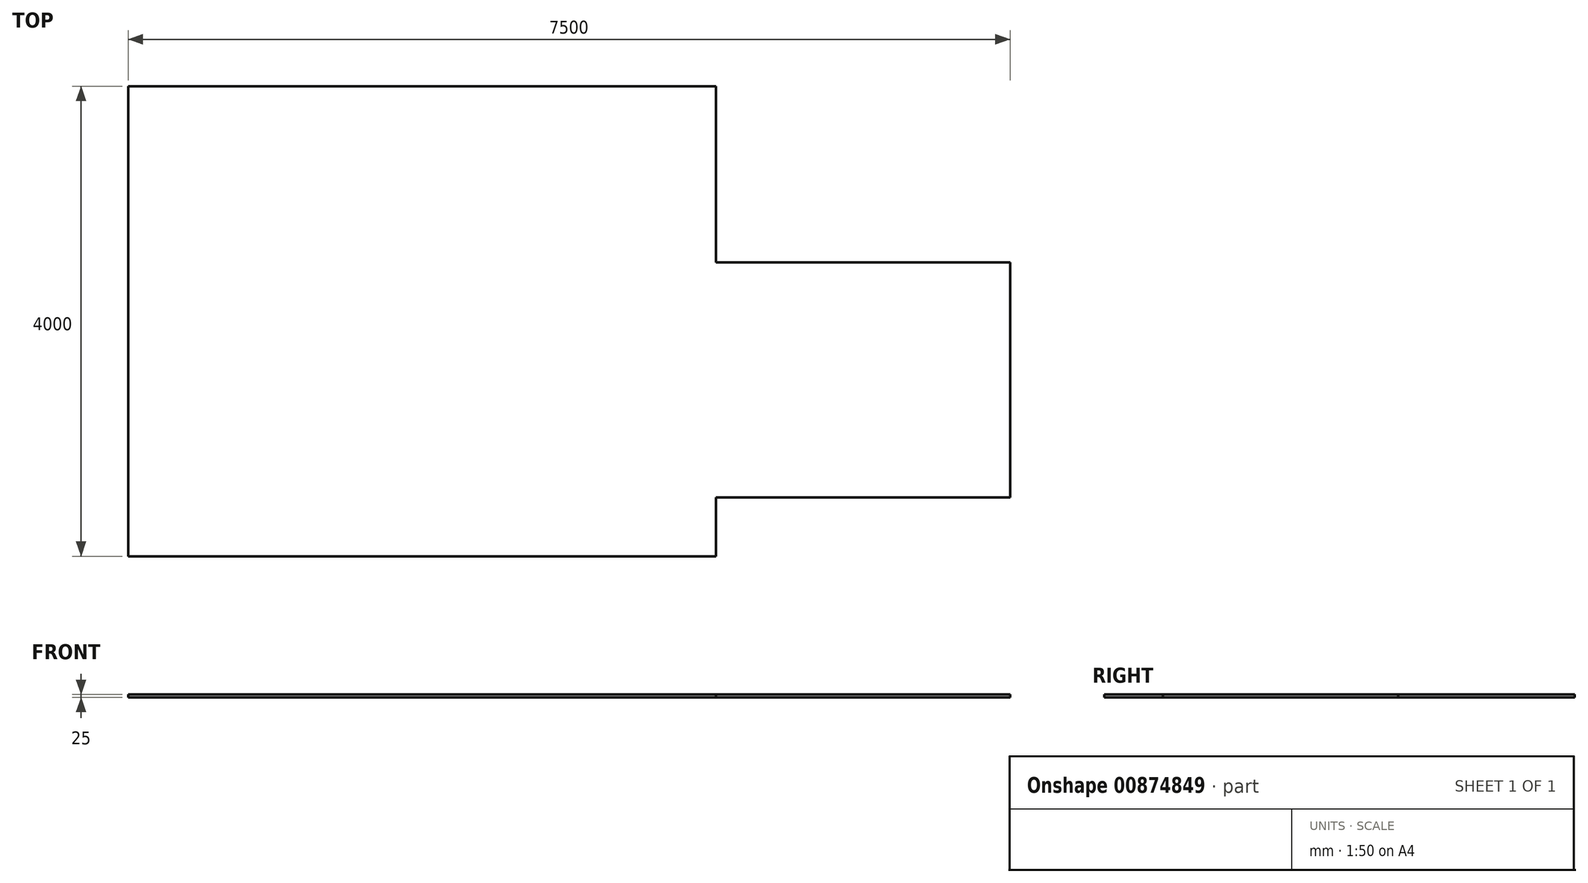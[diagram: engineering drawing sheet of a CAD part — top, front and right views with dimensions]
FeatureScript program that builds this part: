
annotation { "Feature Type Name" : "Feature", "Feature Type Description" : "" }
export const myFeature = defineFeature(function(context is Context, id is Id, definition is map)
    precondition{}
    {
        {
            var Q0;
            Q0=qCreatedBy(makeId("Top.planeOp"),FACE);
            var sketch = newSketch(context, id + "F0", { "sketchPlane" : qUnion([Q0])});
            skLineSegment(sketch, "E0.bottom", {"start": v(0, 0) * mm, "end": v(5000, 0) * mm});
            skLineSegment(sketch, "E0.top", {"start": v(0, 4000) * mm, "end": v(5000, 4000) * mm});
            skLineSegment(sketch, "E0.left", {"start": v(0, 0) * mm, "end": v(0, 4000) * mm});
            skLineSegment(sketch, "E0.right", {"start": v(5000, 0) * mm, "end": v(5000, 4000) * mm});
            skLineSegment(sketch, "E1.bottom", {"start": v(5000, 500) * mm, "end": v(7500, 500) * mm});
            skLineSegment(sketch, "E1.top", {"start": v(5000, 2500) * mm, "end": v(7500, 2500) * mm});
            skLineSegment(sketch, "E1.left", {"start": v(5000, 500) * mm, "end": v(5000, 2500) * mm});
            skLineSegment(sketch, "E1.right", {"start": v(7500, 500) * mm, "end": v(7500, 2500) * mm});
            skSolve(sketch);
        }
        {
            var Q0;
            Q0 = qSketchRegion(id + "F0", true);
            extrude(context, id + "F1", {"entities" : qUnion([Q0]), "depth" : 25 * mm, "offsetDistance" : 25 * mm});
        }
    });
